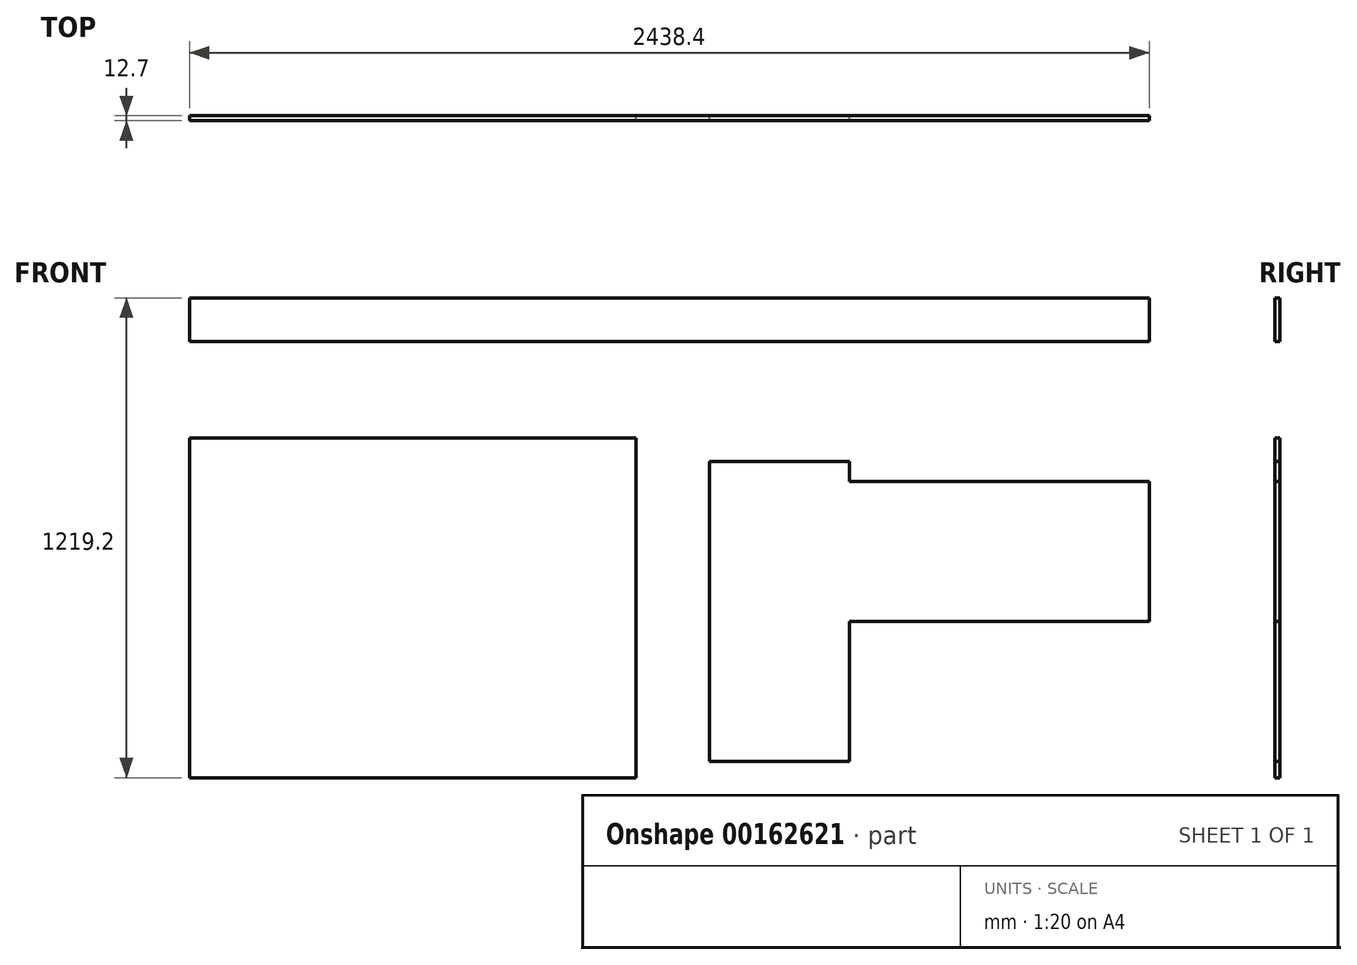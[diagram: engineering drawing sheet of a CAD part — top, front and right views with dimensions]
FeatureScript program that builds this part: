
annotation { "Feature Type Name" : "Feature", "Feature Type Description" : "" }
export const myFeature = defineFeature(function(context is Context, id is Id, definition is map)
    precondition{}
    {
        {
            var Q0;
            Q0=qCreatedBy(makeId("Front.planeOp"),FACE);
            var sketch = newSketch(context, id + "F0", { "sketchPlane" : qUnion([Q0])});
            skLineSegment(sketch, "E0.bottom", {"start": v(0, 0) * mm, "end": v(2438.4, 0) * mm});
            skLineSegment(sketch, "E0.top", {"start": v(0, 1219.2) * mm, "end": v(2438.4, 1219.2) * mm});
            skLineSegment(sketch, "E0.left", {"start": v(0, 0) * mm, "end": v(0, 1219.2) * mm});
            skLineSegment(sketch, "E0.right", {"start": v(2438.4, 0) * mm, "end": v(2438.4, 1219.2) * mm});
            skLineSegment(sketch, "E1.top", {"start": v(0, 1108.08) * mm, "end": v(2438.4, 1108.08) * mm});
            skLineSegment(sketch, "E1.left", {"start": v(0, 1219.2) * mm, "end": v(0, 1108.08) * mm});
            skLineSegment(sketch, "E1.right", {"start": v(2438.4, 1219.2) * mm, "end": v(2438.4, 1108.08) * mm});
            skLineSegment(sketch, "E2.bottom", {"start": v(0, 1108.08) * mm, "end": v(1573.21, 1108.08) * mm});
            skLineSegment(sketch, "E2.top", {"start": v(0, 996.95) * mm, "end": v(1573.21, 996.95) * mm});
            skLineSegment(sketch, "E2.left", {"start": v(0, 1108.08) * mm, "end": v(0, 996.95) * mm});
            skLineSegment(sketch, "E2.right", {"start": v(1573.21, 1108.08) * mm, "end": v(1573.21, 996.95) * mm});
            skLineSegment(sketch, "E3.bottom", {"start": v(2438.4, 1108.08) * mm, "end": v(1676.4, 1108.08) * mm});
            skLineSegment(sketch, "E3.top", {"start": v(2438.4, 752.48) * mm, "end": v(1676.4, 752.48) * mm});
            skLineSegment(sketch, "E3.left", {"start": v(2438.4, 1108.08) * mm, "end": v(2438.4, 752.48) * mm});
            skLineSegment(sketch, "E3.right", {"start": v(1676.4, 1108.08) * mm, "end": v(1676.4, 752.48) * mm});
            skLineSegment(sketch, "E4.top", {"start": v(2438.4, 396.88) * mm, "end": v(1676.4, 396.88) * mm});
            skLineSegment(sketch, "E4.left", {"start": v(2438.4, 752.48) * mm, "end": v(2438.4, 396.88) * mm});
            skLineSegment(sketch, "E4.right", {"start": v(1676.4, 752.48) * mm, "end": v(1676.4, 396.88) * mm});
            skLineSegment(sketch, "E5.top", {"start": v(2438.4, 41.28) * mm, "end": v(1676.4, 41.28) * mm});
            skLineSegment(sketch, "E5.left", {"start": v(2438.4, 396.88) * mm, "end": v(2438.4, 41.28) * mm});
            skLineSegment(sketch, "E5.right", {"start": v(1676.4, 396.88) * mm, "end": v(1676.4, 41.28) * mm});
            skLineSegment(sketch, "E6.bottom", {"start": v(0, 431.8) * mm, "end": v(1135.08, 431.8) * mm});
            skLineSegment(sketch, "E6.top", {"start": v(0, 0) * mm, "end": v(1135.08, 0) * mm});
            skLineSegment(sketch, "E6.left", {"start": v(0, 431.8) * mm, "end": v(0, 0) * mm});
            skLineSegment(sketch, "E6.right", {"start": v(1135.08, 431.8) * mm, "end": v(1135.08, 0) * mm});
            skLineSegment(sketch, "E7.bottom", {"start": v(0, 863.6) * mm, "end": v(1135.08, 863.6) * mm});
            skLineSegment(sketch, "E7.left", {"start": v(0, 863.6) * mm, "end": v(0, 431.8) * mm});
            skLineSegment(sketch, "E7.right", {"start": v(1135.08, 863.6) * mm, "end": v(1135.08, 431.8) * mm});
            skLineSegment(sketch, "E8.bottom", {"start": v(1676.4, 41.28) * mm, "end": v(1320.8, 41.28) * mm});
            skLineSegment(sketch, "E8.top", {"start": v(1676.4, 803.28) * mm, "end": v(1320.8, 803.28) * mm});
            skLineSegment(sketch, "E8.left", {"start": v(1676.4, 41.28) * mm, "end": v(1676.4, 803.28) * mm});
            skLineSegment(sketch, "E8.right", {"start": v(1320.8, 41.28) * mm, "end": v(1320.8, 803.28) * mm});
            skSolve(sketch);
        }
        {
            var Q0;
            Q0=makeQuery(id+"F0.imprint","IMPRINT",FACE,{"disambiguationData":[TD([[makeQuery(id+"F0.imprint","IMPRINT",EDGE,{"derivedFrom":sQuery(id+"F0.wireOp",EDGE,"E7.bottom")}),-1.0]])]});
            var Q1;
            Q1=makeQuery(id+"F0.imprint","IMPRINT",FACE,{"disambiguationData":[TD([[makeQuery(id+"F0.imprint","IMPRINT",EDGE,{"derivedFrom":sQuery(id+"F0.wireOp",EDGE,"E0.bottom")}),1.0]])]});
            var Q2;
            Q2=makeQuery(id+"F0.imprint","IMPRINT",FACE,{"disambiguationData":[TD([[makeQuery(id+"F0.imprint","IMPRINT",EDGE,{"derivedFrom":sQuery(id+"F0.wireOp",EDGE,"E2.bottom")}),-1.0]])]});
            var Q3;
            Q3=makeQuery(id+"F0.imprint","IMPRINT",FACE,{"disambiguationData":[TD([[makeQuery(id+"F0.imprint","IMPRINT",EDGE,{"derivedFrom":sQuery(id+"F0.wireOp",EDGE,"E0.top")}),-1.0]])]});
            var Q4;
            Q4=makeQuery(id+"F0.imprint","IMPRINT",FACE,{"disambiguationData":[TD([[makeQuery(id+"F0.imprint","IMPRINT",EDGE,{"derivedFrom":sQuery(id+"F0.wireOp",EDGE,"E3.bottom")}),1.0]])]});
            var Q5;
            {var subQ0=sQuery(id+"F0.wireOp",EDGE,"E3.top");Q5=makeQuery(id+"F0.imprint","IMPRINT",FACE,{"disambiguationData":[TD([[makeQuery(id+"F0.imprint","IMPRINT",EDGE,{"derivedFrom":subQ0}),1.0]])]});}
            var Q6;
            {var subQ3=sQuery(id+"F0.wireOp",EDGE,"E8.bottom");Q6=makeQuery(id+"F0.imprint","IMPRINT",FACE,{"disambiguationData":[TD([[makeQuery(id+"F0.imprint","IMPRINT",EDGE,{"derivedFrom":subQ3}),-1.0]])]});}
            var Q7;
            Q7=makeQuery(id+"F0.imprint","IMPRINT",FACE,{"disambiguationData":[TD([[makeQuery(id+"F0.imprint","IMPRINT",EDGE,{"derivedFrom":sQuery(id+"F0.wireOp",EDGE,"E6.top")}),1.0]])]});
            extrude(context, id + "F1", {"entities" : qUnion([Q0, Q1, Q2, Q3, Q4, Q5, Q6, Q7]), "depth" : 12.7 * mm});
        }
    });
